AUTODESK INVENTOR PART (.ipt)
format: ipt  version: 2016 (Build 200138000, 138)  size: 112,128 bytes
history: native  units: in
note: dims shown in document units (in); Inventor stores cm internally (conversion verified against a paired STEP export)
features: extrude x1, fillet x1, sketch x1
ambient origin geometry x8: Origin, YZ Plane, XZ Plane, XY Plane, X Axis, Y Axis, Z Axis, Center Point
bodies: Solid1 (feature_tree)
feature tree (3):
  extrude  "Extrusion1"  Depth=0.125in
  fillet  "Fillet1"  Radius=2.0in
  sketch  "Sketch1"  dims[d0=2.0in d4=1.0994in d5=2.0in d6=0.25in d7=1.0in d8=0.2656in d9=0.2656in d10=0.5in d11=1.5in d12=0.5in d13=0.5in d14=0.25in d15=0.0in d16=0.125in]
